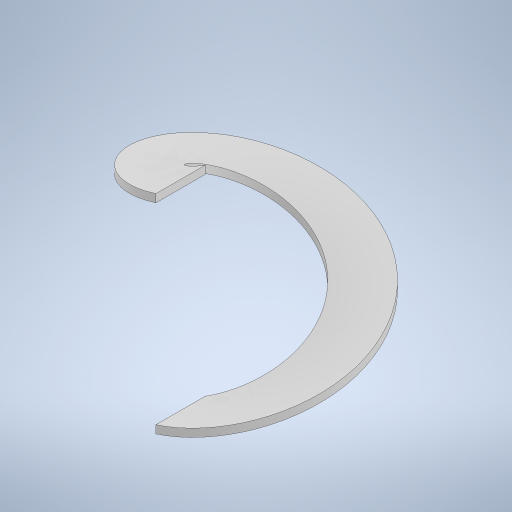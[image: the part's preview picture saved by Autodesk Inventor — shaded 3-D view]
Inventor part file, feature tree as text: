
AUTODESK INVENTOR PART (.ipt)
format: ipt  version: 2024 (Build 280153000, 153)  size: 252,416 bytes
history: native  units: mm
features: sketch x3, plane x1, helix x1
ambient origin geometry x8: Origin, YZ Plane, XZ Plane, XY Plane, X Axis, Y Axis, Z Axis, Center Point
bodies: Solid1 (feature_tree)
feature tree (5):
  sketch  "Sketch1"  dims[d1=6.0mm]
  plane  "Work Plane1"
  sketch  "Sketch2"  dims[d2=150.0mm]
  helix  "Coil1"  [1 undecoded]
  sketch  "Sketch3"  dims[d3=150.0mm d4=150.0mm d5=10.0mm d6=10.0mm d7=0.0mm d8=90.0deg d9=90.0deg d10=0.0mm d11=0.0mm d12=76.1mm d13=38.05mm d14=75.0mm d15=6.0mm]
note: 1 required parameter value undecoded (feature->parameter linkage not recoverable at this tier; creation-order binding heuristic only, values carry confidence <= 0.55)
